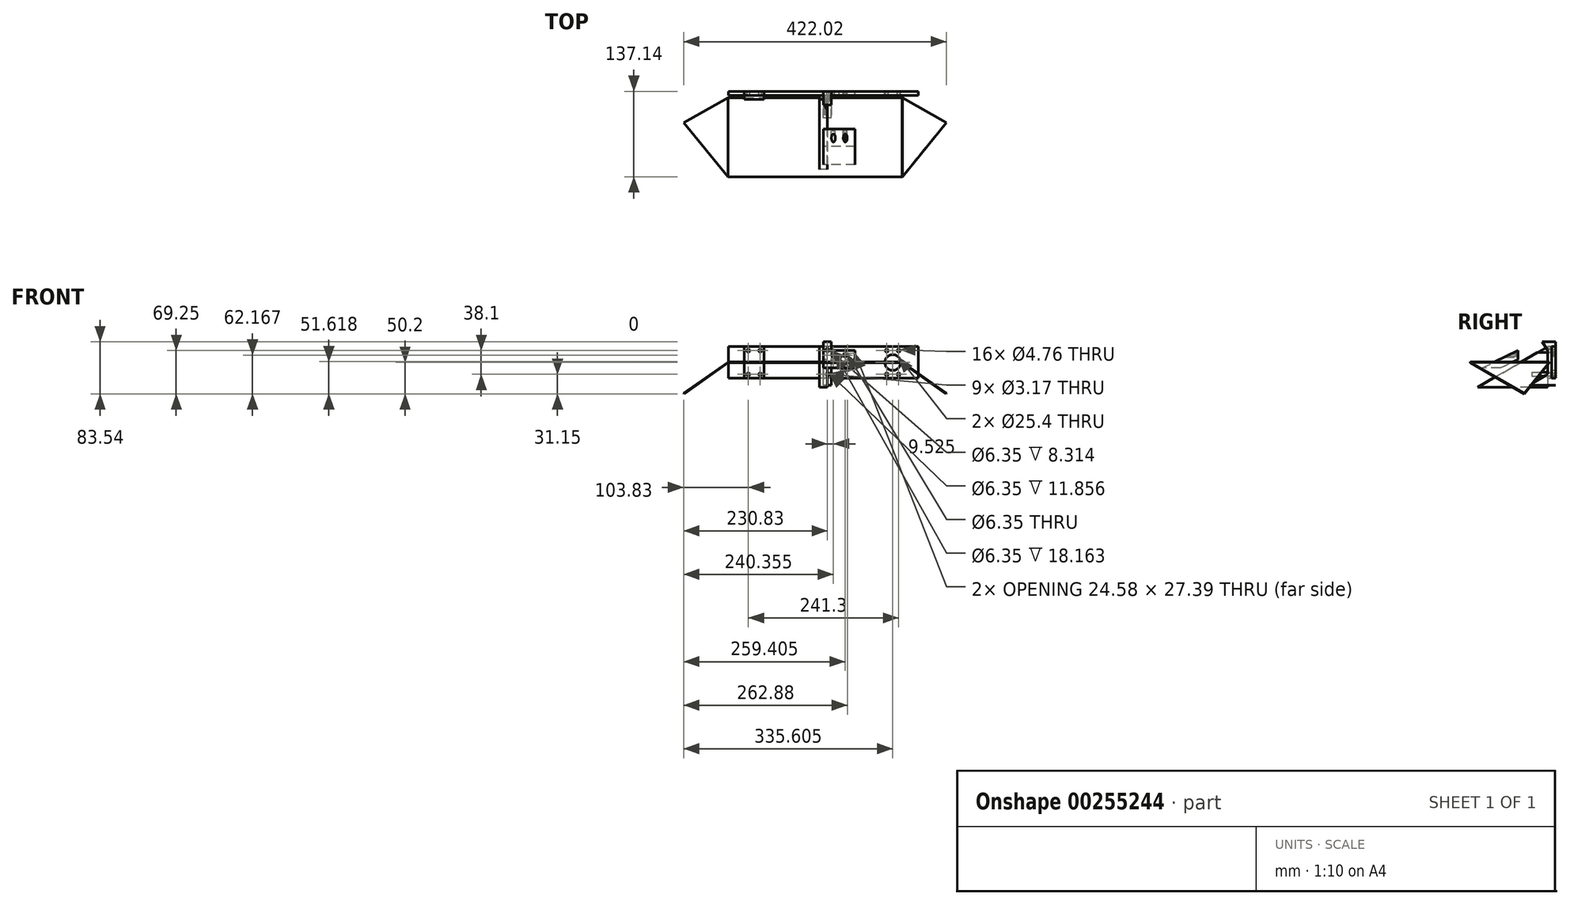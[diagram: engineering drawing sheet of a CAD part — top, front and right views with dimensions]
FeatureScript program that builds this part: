
annotation { "Feature Type Name" : "Feature", "Feature Type Description" : "" }
export const myFeature = defineFeature(function(context is Context, id is Id, definition is map)
    precondition{}
    {
        {
            var Q0;
            Q0=qCreatedBy(makeId("Front.planeOp"),FACE);
            var sketch = newSketch(context, id + "F0", { "sketchPlane" : qUnion([Q0])});
            skLineSegment(sketch, "E0.bottom", {"start": v(152.4, -25.4) * mm, "end": v(-152.4, -25.4) * mm});
            skLineSegment(sketch, "E0.top", {"start": v(152.4, 25.4) * mm, "end": v(-152.4, 25.4) * mm});
            skLineSegment(sketch, "E0.left", {"start": v(152.4, -25.4) * mm, "end": v(152.4, 25.4) * mm});
            skLineSegment(sketch, "E0.right", {"start": v(-152.4, -25.4) * mm, "end": v(-152.4, 25.4) * mm});
            skPoint(sketch, "E0.middle", {"position": v(0, 0) * mm});
            skCircle(sketch, "E1", {"center": v(-120.65, -19.05) * mm, "radius": 2.38 * mm});
            skCircle(sketch, "E2", {"center": v(-101.6, -19.05) * mm, "radius": 2.38 * mm});
            skLineSegment(sketch, "E3", {"start": v(0, 25.4) * mm, "end": v(0, -25.4) * mm, "construction": true});
            skCircle(sketch, "E4.MirrorC", {"center": v(120.65, -19.05) * mm, "radius": 2.38 * mm});
            skCircle(sketch, "E5.MirrorC", {"center": v(101.6, -19.05) * mm, "radius": 2.38 * mm});
            skLineSegment(sketch, "E6", {"start": v(-152.4, 0) * mm, "end": v(152.4, 0) * mm, "construction": true});
            skCircle(sketch, "E7.MirrorC", {"center": v(-120.65, 19.05) * mm, "radius": 2.38 * mm});
            skCircle(sketch, "E8.MirrorC", {"center": v(-101.6, 19.05) * mm, "radius": 2.38 * mm});
            skCircle(sketch, "E9.MirrorC", {"center": v(101.6, 19.05) * mm, "radius": 2.38 * mm});
            skCircle(sketch, "E10.MirrorC", {"center": v(120.65, 19.05) * mm, "radius": 2.38 * mm});
            skLineSegment(sketch, "E11", {"start": v(-120.65, -19.05) * mm, "end": v(-101.6, -19.05) * mm, "construction": true});
            skCircle(sketch, "E12", {"center": v(-111.12, 0) * mm, "radius": 12.7 * mm});
            skPoint(sketch, "E12.centerSnap0", {"position": v(-111.12, -19.05) * mm});
            skCircle(sketch, "E13", {"center": v(0, 0) * mm, "radius": 12.7 * mm});
            skCircle(sketch, "E14", {"center": v(-38.1, 0) * mm, "radius": 12.7 * mm});
            skPoint(sketch, "E14.centerSnap0", {"position": v(-38.1, 12.7) * mm});
            skCircle(sketch, "E15.MirrorC", {"center": v(38.1, 0) * mm, "radius": 12.7 * mm});
            skCircle(sketch, "E16.MirrorC", {"center": v(111.12, 0) * mm, "radius": 12.7 * mm});
            skSolve(sketch);
        }
        {
            var Q0;
            Q0=makeQuery(id+"F0.imprint","IMPRINT",FACE,{"disambiguationData":[TD([[makeQuery(id+"F0.imprint","IMPRINT",EDGE,{"derivedFrom":sQuery(id+"F0.wireOp",EDGE,"E0.bottom")}),-1.0]])]});
            var sketch = newSketch(context, id + "F1", { "sketchPlane" : qUnion([Q0])});
            skCircle(sketch, "E17.0", {"center": v(-120.65, -19.05) * mm, "radius": 2.38 * mm});
            skCircle(sketch, "E17.1", {"center": v(-101.6, -19.05) * mm, "radius": 2.38 * mm});
            skCircle(sketch, "E17.2", {"center": v(101.6, -19.05) * mm, "radius": 2.38 * mm});
            skCircle(sketch, "E17.3", {"center": v(120.65, -19.05) * mm, "radius": 2.38 * mm});
            skLineSegment(sketch, "E18.bottom", {"start": v(-127, -25.4) * mm, "end": v(-95.25, -25.4) * mm});
            skLineSegment(sketch, "E18.top", {"start": v(-127, 25.4) * mm, "end": v(-95.25, 25.4) * mm});
            skLineSegment(sketch, "E18.left", {"start": v(-127, -25.4) * mm, "end": v(-127, 25.4) * mm});
            skLineSegment(sketch, "E18.right", {"start": v(-95.25, -25.4) * mm, "end": v(-95.25, 25.4) * mm});
            skLineSegment(sketch, "E19", {"start": v(0, 26) * mm, "end": v(0, -25.22) * mm, "construction": true});
            skLineSegment(sketch, "E20.MirrorCS", {"start": v(95.25, -25.4) * mm, "end": v(95.25, 25.4) * mm});
            skLineSegment(sketch, "E21.MirrorCS", {"start": v(127, 25.4) * mm, "end": v(95.25, 25.4) * mm});
            skLineSegment(sketch, "E22.MirrorCS", {"start": v(127, -25.4) * mm, "end": v(127, 25.4) * mm});
            skLineSegment(sketch, "E23.MirrorCS", {"start": v(127, -25.4) * mm, "end": v(95.25, -25.4) * mm});
            skSolve(sketch);
        }
        {
            var Q0;
            Q0=makeQuery(id+"F0.imprint","IMPRINT",FACE,{"disambiguationData":[TD([[makeQuery(id+"F0.imprint","IMPRINT",EDGE,{"derivedFrom":sQuery(id+"F0.wireOp",EDGE,"E0.bottom")}),-1.0]])]});
            var Q1;
            Q1=makeQuery(id+"F0.imprint","IMPRINT",FACE,{"disambiguationData":[TD([[makeQuery(id+"F0.imprint","IMPRINT",EDGE,{"derivedFrom":sQuery(id+"F0.wireOp",EDGE,"E12")}),1.0]])]});
            var Q2;
            Q2=makeQuery(id+"F0.imprint","IMPRINT",FACE,{"disambiguationData":[TD([[makeQuery(id+"F0.imprint","IMPRINT",EDGE,{"derivedFrom":sQuery(id+"F0.wireOp",EDGE,"E14")}),1.0]])]});
            var Q3;
            Q3=makeQuery(id+"F0.imprint","IMPRINT",FACE,{"disambiguationData":[TD([[makeQuery(id+"F0.imprint","IMPRINT",EDGE,{"derivedFrom":sQuery(id+"F0.wireOp",EDGE,"E13")}),1.0]])]});
            var Q4;
            Q4=makeQuery(id+"F0.imprint","IMPRINT",FACE,{"disambiguationData":[TD([[makeQuery(id+"F0.imprint","IMPRINT",EDGE,{"derivedFrom":sQuery(id+"F0.wireOp",EDGE,"E15.MirrorC")}),-1.0]])]});
            var Q5;
            Q5=makeQuery(id+"F0.imprint","IMPRINT",FACE,{"disambiguationData":[TD([[makeQuery(id+"F0.imprint","IMPRINT",EDGE,{"derivedFrom":sQuery(id+"F0.wireOp",EDGE,"E16.MirrorC")}),-1.0]])]});
            extrude(context, id + "F2", {"entities" : qUnion([Q0, Q1, Q2, Q3, Q4, Q5]), "depth" : 6.35 * mm});
        }
        {
            var Q0;
            Q0=makeQuery(id+"F1.imprint","IMPRINT",FACE,{"disambiguationData":[TD([[makeQuery(id+"F1.imprint","IMPRINT",EDGE,{"derivedFrom":sQuery(id+"F1.wireOp",EDGE,"E17.0")}),-1.0]])]});
            var Q1;
            Q1=makeQuery(id+"F1.imprint","IMPRINT",FACE,{"disambiguationData":[TD([[makeQuery(id+"F1.imprint","IMPRINT",EDGE,{"derivedFrom":makeQuery(id+"F0.imprint","IMPRINT",EDGE,{"derivedFrom":sQuery(id+"F0.wireOp",EDGE,"E12")})}),1.0]])]});
            extrude(context, id + "F3", {"entities" : qUnion([Q0, Q1]), "depth" : 12.7 * mm});
        }
        {
            var Q0;
            Q0=qCreatedBy(makeId("Right.planeOp"),FACE);
            var sketch = newSketch(context, id + "F4", { "sketchPlane" : qUnion([Q0])});
            skLineSegment(sketch, "E24.0.2", {"start": v(-12.7, -25.4) * mm, "end": v(-12.7, 25.4) * mm});
            skLineSegment(sketch, "E25", {"start": v(-12.7, -25.4) * mm, "end": v(-12.7, -39.69) * mm});
            skLineSegment(sketch, "E26", {"start": v(-12.7, -39.69) * mm, "end": v(-125.43, -39.69) * mm});
            skLineSegment(sketch, "E27", {"start": v(-125.43, -39.69) * mm, "end": v(-12.7, 25.4) * mm});
            skPoint(sketch, "E28.0", {"position": v(0, 0) * mm});
            skLineSegment(sketch, "E28.1.0", {"start": v(0, -25.4) * mm, "end": v(0, 25.4) * mm});
            skLineSegment(sketch, "E28.1.1", {"start": v(0, 25.4) * mm, "end": v(-12.7, 25.4) * mm});
            skLineSegment(sketch, "E28.1.2", {"start": v(-12.7, 25.4) * mm, "end": v(-12.7, -25.4) * mm});
            skLineSegment(sketch, "E28.1.3", {"start": v(-12.7, -25.4) * mm, "end": v(0, -25.4) * mm});
            skSolve(sketch);
        }
        {
            var Q0;
            Q0=qSketchRegion(id+"F4",true);
            extrude(context, id + "F5", {"entities" : qUnion([Q0]), "operationType" : NewBodyOperationType.ADD, "depth" : 12.7 * mm, "symmetric" : true});
        }
        {
            var Q0;
            Q0=qCreatedBy(makeId("Top.planeOp"),FACE);
            var sketch = newSketch(context, id + "F6", { "sketchPlane" : qUnion([Q0])});
            skLineSegment(sketch, "E29.bottom", {"start": v(-153.17, -10.14) * mm, "end": v(126.23, -10.14) * mm});
            skLineSegment(sketch, "E29.top", {"start": v(-153.17, -137.14) * mm, "end": v(126.23, -137.14) * mm});
            skLineSegment(sketch, "E29.left", {"start": v(-153.17, -10.14) * mm, "end": v(-153.17, -137.14) * mm});
            skLineSegment(sketch, "E29.right", {"start": v(126.23, -10.14) * mm, "end": v(126.23, -137.14) * mm});
            skSolve(sketch);
        }
        {
            var Q0;
            Q0=qSketchRegion(id+"F6",true);
            extrude(context, id + "F7", {"entities" : qUnion([Q0]), "depth" : 1.27 * mm, "symmetric" : true});
        }
        {
            var Q0;
            Q0=qCreatedBy(makeId("Top.planeOp"),FACE);
            var sketch = newSketch(context, id + "F8", { "sketchPlane" : qUnion([Q0])});
            skLineSegment(sketch, "E30.0", {"start": v(-153.17, -10.14) * mm, "end": v(-153.17, -137.14) * mm});
            skLineSegment(sketch, "E31", {"start": v(-153.17, -137.14) * mm, "end": v(-239.78, -50.53) * mm});
            skLineSegment(sketch, "E32", {"start": v(-239.78, -50.53) * mm, "end": v(-153.17, -10.14) * mm});
            skSolve(sketch);
        }
        {
            var Q0;
            Q0=qSketchRegion(id+"F8",true);
            extrude(context, id + "F9", {"entities" : qUnion([Q0]), "depth" : 1.27 * mm, "symmetric" : true});
        }
        {
            var Q0;
            Q0=makeQuery(id+"F9.opExtrude","SWEPT_BODY",BODY,{"disambiguationData":[OSD([sQuery(id+"F8.wireOp",EDGE,"E30.0"),sQuery(id+"F8.wireOp",EDGE,"E31"),sQuery(id+"F8.wireOp",EDGE,"E32")])]});
            transform(context, id + "F10", {"entities" : qUnion([Q0]), "transformType" : TransformType.TRANSLATION_3D, "dx" : 279.4 * mm, "dy" : 0 * mm, "dz" : 0 * mm, "makeCopy" : true});
        }
        {
            var Q0;
            Q0=makeQuery(id+"F10.opPattern","COPY",BODY,{"derivedFrom":makeQuery(id+"F9.opExtrude","SWEPT_BODY",BODY,{"disambiguationData":[OSD([sQuery(id+"F8.wireOp",EDGE,"E30.0"),sQuery(id+"F8.wireOp",EDGE,"E31"),sQuery(id+"F8.wireOp",EDGE,"E32")])]}),"instanceName":"1"});
            var Q1;
            Q1=sQuery(id+"F6.wireOp",EDGE,"E29.right");
            transform(context, id + "F11", {"entities" : qUnion([Q0]), "transformType" : TransformType.ROTATION, "transformAxis" : qUnion([Q1]), "angle" : 145 * degree, "makeCopy" : false});
        }
        {
            var Q0;
            Q0=makeQuery(id+"F9.opExtrude","SWEPT_BODY",BODY,{"disambiguationData":[OSD([sQuery(id+"F8.wireOp",EDGE,"E30.0"),sQuery(id+"F8.wireOp",EDGE,"E31"),sQuery(id+"F8.wireOp",EDGE,"E32")])]});
            var Q1;
            Q1=sQuery(id+"F6.wireOp",EDGE,"E29.left");
            transform(context, id + "F12", {"entities" : qUnion([Q0]), "transformType" : TransformType.ROTATION, "transformAxis" : qUnion([Q1]), "angle" : 35 * degree, "makeCopy" : false});
        }
        {
            var Q0;
            Q0=makeQuery(id+"F0.imprint","IMPRINT",FACE,{"disambiguationData":[TD([[makeQuery(id+"F0.imprint","IMPRINT",EDGE,{"derivedFrom":sQuery(id+"F0.wireOp",EDGE,"E0.bottom")}),-1.0]])]});
            var Q1;
            Q1=makeQuery(id+"F0.imprint","IMPRINT",FACE,{"disambiguationData":[TD([[makeQuery(id+"F0.imprint","IMPRINT",EDGE,{"derivedFrom":sQuery(id+"F0.wireOp",EDGE,"E12")}),1.0]])]});
            var Q2;
            Q2=makeQuery(id+"F0.imprint","IMPRINT",FACE,{"disambiguationData":[TD([[makeQuery(id+"F0.imprint","IMPRINT",EDGE,{"derivedFrom":sQuery(id+"F0.wireOp",EDGE,"E7.MirrorC")}),-1.0]])]});
            var Q3;
            Q3=makeQuery(id+"F0.imprint","IMPRINT",FACE,{"disambiguationData":[TD([[makeQuery(id+"F0.imprint","IMPRINT",EDGE,{"derivedFrom":sQuery(id+"F0.wireOp",EDGE,"E8.MirrorC")}),-1.0]])]});
            var Q4;
            Q4=makeQuery(id+"F0.imprint","IMPRINT",FACE,{"disambiguationData":[TD([[makeQuery(id+"F0.imprint","IMPRINT",EDGE,{"derivedFrom":sQuery(id+"F0.wireOp",EDGE,"E1")}),1.0]])]});
            var Q5;
            Q5=makeQuery(id+"F0.imprint","IMPRINT",FACE,{"disambiguationData":[TD([[makeQuery(id+"F0.imprint","IMPRINT",EDGE,{"derivedFrom":sQuery(id+"F0.wireOp",EDGE,"E2")}),1.0]])]});
            var Q6;
            Q6=makeQuery(id+"F0.imprint","IMPRINT",FACE,{"disambiguationData":[TD([[makeQuery(id+"F0.imprint","IMPRINT",EDGE,{"derivedFrom":sQuery(id+"F0.wireOp",EDGE,"E14")}),1.0]])]});
            var Q7;
            Q7=makeQuery(id+"F0.imprint","IMPRINT",FACE,{"disambiguationData":[TD([[makeQuery(id+"F0.imprint","IMPRINT",EDGE,{"derivedFrom":sQuery(id+"F0.wireOp",EDGE,"E13")}),1.0]])]});
            var Q8;
            Q8=makeQuery(id+"F0.imprint","IMPRINT",FACE,{"disambiguationData":[TD([[makeQuery(id+"F0.imprint","IMPRINT",EDGE,{"derivedFrom":sQuery(id+"F0.wireOp",EDGE,"E15.MirrorC")}),-1.0]])]});
            var Q9;
            Q9=makeQuery(id+"F0.imprint","IMPRINT",FACE,{"disambiguationData":[TD([[makeQuery(id+"F0.imprint","IMPRINT",EDGE,{"derivedFrom":sQuery(id+"F0.wireOp",EDGE,"E16.MirrorC")}),-1.0]])]});
            var Q10;
            Q10=makeQuery(id+"F0.imprint","IMPRINT",FACE,{"disambiguationData":[TD([[makeQuery(id+"F0.imprint","IMPRINT",EDGE,{"derivedFrom":sQuery(id+"F0.wireOp",EDGE,"E9.MirrorC")}),1.0]])]});
            var Q11;
            Q11=makeQuery(id+"F0.imprint","IMPRINT",FACE,{"disambiguationData":[TD([[makeQuery(id+"F0.imprint","IMPRINT",EDGE,{"derivedFrom":sQuery(id+"F0.wireOp",EDGE,"E5.MirrorC")}),-1.0]])]});
            var Q12;
            Q12=makeQuery(id+"F0.imprint","IMPRINT",FACE,{"disambiguationData":[TD([[makeQuery(id+"F0.imprint","IMPRINT",EDGE,{"derivedFrom":sQuery(id+"F0.wireOp",EDGE,"E4.MirrorC")}),-1.0]])]});
            var Q13;
            Q13=makeQuery(id+"F0.imprint","IMPRINT",FACE,{"disambiguationData":[TD([[makeQuery(id+"F0.imprint","IMPRINT",EDGE,{"derivedFrom":sQuery(id+"F0.wireOp",EDGE,"E10.MirrorC")}),1.0]])]});
            extrude(context, id + "F13", {"entities" : qUnion([Q0, Q1, Q2, Q3, Q4, Q5, Q6, Q7, Q8, Q9, Q10, Q11, Q12, Q13]), "depth" : 6.35 * mm});
        }
        {
            var Q0;
            Q0=qCreatedBy(makeId("Right.planeOp"),FACE);
            var sketch = newSketch(context, id + "F14", { "sketchPlane" : qUnion([Q0])});
            skLineSegment(sketch, "E33", {"start": v(-117.6, -8.67) * mm, "end": v(-60.45, 19.03) * mm});
            skLineSegment(sketch, "E34", {"start": v(-60.45, 4.92) * mm, "end": v(-88.48, -8.67) * mm});
            skLineSegment(sketch, "E35", {"start": v(-88.48, -8.67) * mm, "end": v(-117.6, -8.67) * mm});
            skLineSegment(sketch, "E36", {"start": v(-60.45, 19.03) * mm, "end": v(-60.45, 11.97) * mm});
            skLineSegment(sketch, "E37", {"start": v(-60.45, 11.97) * mm, "end": v(-60.45, 4.92) * mm});
            skSolve(sketch);
        }
        {
            var Q0;
            Q0=makeQuery(id+"F14.imprint","IMPRINT",FACE,{"disambiguationData":[TD([[makeQuery(id+"F14.imprint","IMPRINT",EDGE,{"derivedFrom":sQuery(id+"F14.wireOp",EDGE,"E33")}),-1.0]])]});
            extrude(context, id + "F15", {"entities" : qUnion([Q0]), "depth" : 50.8 * mm});
        }
        {
            var Q0;
            Q0=qCreatedBy(makeId("Front.planeOp"),FACE);
            var sketch = newSketch(context, id + "F16", { "sketchPlane" : qUnion([Q0])});
            skLineSegment(sketch, "E38.0", {"start": v(0, -8.67) * mm, "end": v(0, 19.03) * mm});
            skLineSegment(sketch, "E38.1", {"start": v(50.8, 19.03) * mm, "end": v(0, 19.03) * mm});
            skLineSegment(sketch, "E38.2", {"start": v(50.8, -8.67) * mm, "end": v(50.8, 19.03) * mm});
            skCircle(sketch, "E39", {"center": v(15.88, 11.97) * mm, "radius": 3.18 * mm});
            skLineSegment(sketch, "E40", {"start": v(25.4, 19.03) * mm, "end": v(25.4, -8.6) * mm, "construction": true});
            skPoint(sketch, "E40.endSnap0", {"position": v(25.4, 19.03) * mm});
            skCircle(sketch, "E41", {"center": v(15.88, 11.97) * mm, "radius": 1.59 * mm});
            skCircle(sketch, "E42.MirrorC", {"center": v(34.93, 11.97) * mm, "radius": 3.18 * mm});
            skCircle(sketch, "E43.MirrorC", {"center": v(34.93, 11.97) * mm, "radius": 1.59 * mm});
            skSolve(sketch);
        }
        {
            var Q0;
            Q0=makeQuery(id+"F16.imprint","IMPRINT",FACE,{"disambiguationData":[TD([[makeQuery(id+"F16.imprint","IMPRINT",EDGE,{"derivedFrom":sQuery(id+"F16.wireOp",EDGE,"E41")}),1.0]])]});
            var Q1;
            Q1=makeQuery(id+"F16.imprint","IMPRINT",FACE,{"disambiguationData":[TD([[makeQuery(id+"F16.imprint","IMPRINT",EDGE,{"derivedFrom":sQuery(id+"F16.wireOp",EDGE,"E43.MirrorC")}),-1.0]])]});
            extrude(context, id + "F17", {"entities" : qUnion([Q0, Q1]), "operationType" : NewBodyOperationType.REMOVE, "endBound" : BoundingType.THROUGH_ALL, "depth" : 25.4 * mm});
        }
        {
            var Q0;
            Q0=makeQuery(id+"F16.imprint","IMPRINT",FACE,{"disambiguationData":[TD([[makeQuery(id+"F16.imprint","IMPRINT",EDGE,{"derivedFrom":sQuery(id+"F16.wireOp",EDGE,"E39")}),1.0]])]});
            var Q1;
            Q1=makeQuery(id+"F16.imprint","IMPRINT",FACE,{"disambiguationData":[TD([[makeQuery(id+"F16.imprint","IMPRINT",EDGE,{"derivedFrom":sQuery(id+"F16.wireOp",EDGE,"E42.MirrorC")}),-1.0]])]});
            var Q2;
            Q2=makeQuery(id+"F15.opExtrude","SWEPT_FACE",FACE,{"disambiguationData":[OSD([sQuery(id+"F14.wireOp",EDGE,"E33")])]});
            var Q3;
            Q3=makeQuery(id+"F15.opExtrude","SWEPT_FACE",FACE,{"disambiguationData":[OSD([sQuery(id+"F14.wireOp",EDGE,"E33")])]});
            extrude(context, id + "F18", {"entities" : qUnion([Q0, Q1]), "operationType" : NewBodyOperationType.REMOVE, "endBoundEntityFace" : qUnion([Q2]), "depth" : 101.6 * mm, "hasSecondDirection" : true, "secondDirectionOppositeDirection" : false, "secondDirectionBoundEntityFace" : qUnion([Q3]), "secondDirectionDepth" : 63.5 * mm});
        }
        {
            var Q0;
            Q0=qCreatedBy(makeId("Right.planeOp"),FACE);
            var sketch = newSketch(context, id + "F19", { "sketchPlane" : qUnion([Q0])});
            skLineSegment(sketch, "E44.0", {"start": v(0, 25.4) * mm, "end": v(0, -25.4) * mm, "construction": true});
            skLineSegment(sketch, "E45", {"start": v(-12.7, 19.05) * mm, "end": v(9.1, 19.05) * mm, "construction": true});
            skLineSegment(sketch, "E46", {"start": v(-12.7, -19.05) * mm, "end": v(8.92, -19.05) * mm, "construction": true});
            skLineSegment(sketch, "E47", {"start": v(-92.16, -39.69) * mm, "end": v(110.36, -39.69) * mm, "construction": true});
            skLineSegment(sketch, "E48", {"start": v(-93.21, 39.69) * mm, "end": v(122.69, 39.69) * mm, "construction": true});
            skLineSegment(sketch, "E49", {"start": v(-42.95, -36.51) * mm, "end": v(-15.87, -20.88) * mm});
            skLineSegment(sketch, "E50", {"start": v(-12.7, -15.38) * mm, "end": v(-12.7, 17.25) * mm});
            skLineSegment(sketch, "E51", {"start": v(-13.65, 20.58) * mm, "end": v(-21.52, 33.34) * mm});
            skLineSegment(sketch, "E52", {"start": v(-21.52, 33.34) * mm, "end": v(0, 33.34) * mm});
            skLineSegment(sketch, "E53", {"start": v(0, 33.34) * mm, "end": v(0, -36.51) * mm});
            skLineSegment(sketch, "E54", {"start": v(0, -36.51) * mm, "end": v(-42.95, -36.51) * mm});
            skPoint(sketch, "E55.visualSharp", {"position": v(-12.7, -19.05) * mm});
            skArc(sketch, "E55.filletArc", {"start": v(-15.88, -20.88) * mm, "mid": v(-13.55, -18.56) * mm, "end": v(-12.7, -15.38) * mm});
            skPoint(sketch, "E56.visualSharp", {"position": v(-12.7, 19.05) * mm});
            skArc(sketch, "E56.filletArc", {"start": v(-12.7, 17.25) * mm, "mid": v(-12.94, 18.98) * mm, "end": v(-13.65, 20.58) * mm});
            skSolve(sketch);
        }
        {
            var Q0;
            Q0=makeQuery(id+"F19.imprint","IMPRINT",FACE,{"disambiguationData":[TD([[makeQuery(id+"F19.imprint","IMPRINT",EDGE,{"derivedFrom":sQuery(id+"F19.wireOp",EDGE,"E49")}),-1.0]])]});
            extrude(context, id + "F20", {"entities" : qUnion([Q0]), "depth" : 12.7 * mm});
        }
        {
            var Q0;
            Q0=makeQuery(id+"F20.opExtrude","SWEPT_FACE",FACE,{"disambiguationData":[OSD([sQuery(id+"F19.wireOp",EDGE,"E50")])]});
            var sketch = newSketch(context, id + "F21", { "sketchPlane" : qUnion([Q0])});
            skLineSegment(sketch, "E57", {"start": v(6.35, 17.25) * mm, "end": v(6.35, -15.38) * mm, "construction": true});
            skPoint(sketch, "E58.0", {"position": v(0, 19.05) * mm});
            skPoint(sketch, "E58.1", {"position": v(0, -19.05) * mm});
            skLineSegment(sketch, "E59", {"start": v(6.35, 17.25) * mm, "end": v(6.35, 25.14) * mm, "construction": true});
            skLineSegment(sketch, "E60", {"start": v(6.35, -15.38) * mm, "end": v(6.35, -25.22) * mm, "construction": true});
            skCircle(sketch, "E61", {"center": v(6.35, 19.05) * mm, "radius": 3.18 * mm});
            skCircle(sketch, "E62", {"center": v(6.35, -19.05) * mm, "radius": 3.18 * mm});
            skCircle(sketch, "E63", {"center": v(6.35, 19.05) * mm, "radius": 1.59 * mm});
            skCircle(sketch, "E64", {"center": v(6.35, -19.05) * mm, "radius": 1.59 * mm});
            skSolve(sketch);
        }
        {
            var Q0;
            Q0=makeQuery(id+"F21.imprint","IMPRINT",FACE,{"disambiguationData":[TD([[makeQuery(id+"F21.imprint","IMPRINT",EDGE,{"derivedFrom":sQuery(id+"F21.wireOp",EDGE,"E63")}),1.0]])]});
            var Q1;
            Q1=makeQuery(id+"F21.imprint","IMPRINT",FACE,{"disambiguationData":[TD([[makeQuery(id+"F21.imprint","IMPRINT",EDGE,{"derivedFrom":sQuery(id+"F21.wireOp",EDGE,"E64")}),1.0]])]});
            var Q2;
            Q2=sQuery(id+"F21.wireOp",EDGE,"E63");
            var Q3;
            Q3=sQuery(id+"F21.wireOp",EDGE,"E64");
            extrude(context, id + "F22", {"entities" : qUnion([Q0, Q1]), "operationType" : NewBodyOperationType.REMOVE, "surfaceEntities" : qUnion([Q2, Q3]), "endBound" : BoundingType.THROUGH_ALL, "oppositeDirection" : true, "depth" : 25.4 * mm, "hasSecondDirection" : true, "secondDirectionOppositeDirection" : false, "secondDirectionDepth" : 25.4 * mm});
        }
        {
            var Q0;
            Q0=makeQuery(id+"F21.imprint","IMPRINT",FACE,{"disambiguationData":[TD([[makeQuery(id+"F21.imprint","IMPRINT",EDGE,{"derivedFrom":sQuery(id+"F21.wireOp",EDGE,"E63")}),-1.0]])]});
            var Q1;
            {var subQ0=sQuery(id+"F21.wireOp",EDGE,"E61");var subQ1=makeQuery(id+"F20.opExtrude","SWEPT_EDGE",EDGE,{"disambiguationData":[OSD([sQuery(id+"F19.wireOp",EDGE,"E50"),sQuery(id+"F19.wireOp",EDGE,"E56.filletArc")])]});var subQ2=makeQuery(id+"F21.imprint","INTERSECT",VERTEX,{"disambiguationData":[OD(0.0)],"derivedFrom":[subQ1,subQ0]});Q1=makeQuery(id+"F21.imprint","IMPRINT",FACE,{"disambiguationData":[TD([[makeQuery(id+"F21.imprint","IMPRINT",EDGE,{"disambiguationData":[TD([[subQ2,-1.0]])],"derivedFrom":subQ0}),1.0]])]});}
            var Q2;
            Q2=makeQuery(id+"F21.imprint","IMPRINT",FACE,{"disambiguationData":[TD([[makeQuery(id+"F21.imprint","IMPRINT",EDGE,{"derivedFrom":sQuery(id+"F21.wireOp",EDGE,"E62")}),1.0]])]});
            var Q3;
            Q3=sQuery(id+"F21.wireOp",EDGE,"E61");
            var Q4;
            Q4=sQuery(id+"F21.wireOp",EDGE,"E62");
            extrude(context, id + "F23", {"entities" : qUnion([Q0, Q1, Q2]), "operationType" : NewBodyOperationType.REMOVE, "surfaceEntities" : qUnion([Q3, Q4]), "depth" : 25.4 * mm, "hasSecondDirection" : true, "secondDirectionOppositeDirection" : true, "secondDirectionDepth" : 6.35 * mm});
        }
    });
